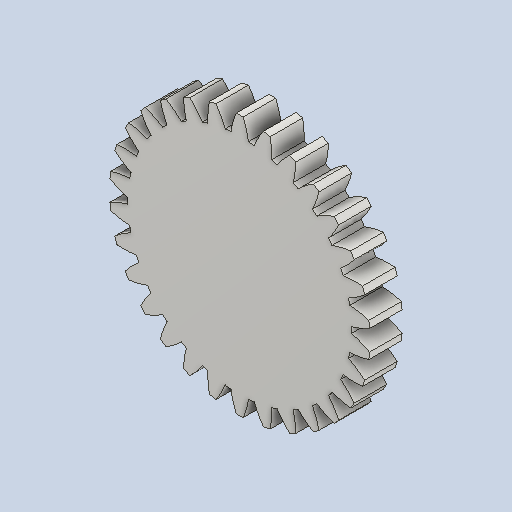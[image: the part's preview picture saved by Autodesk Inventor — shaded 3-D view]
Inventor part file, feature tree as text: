
AUTODESK INVENTOR PART (.ipt)
format: ipt  version: 2024 (Build 280153000, 153)  size: 265,728 bytes
history: native  units: mm (DEFAULTED — no unit token found)
features: plane x3, other x3, extrude x1, sketch x1
ambient origin geometry x8: Origin, YZ Plane, XZ Plane, XY Plane, X Axis, Y Axis, Z Axis, Center Point
bodies: Solid1 (feature_tree)
feature tree (8):
  extrude  "Extrusion1"  Depth=20.0mm TaperAngle=0.0deg
  plane  "Work Plane2"
  plane  "Work Plane8"
  plane  "Work Plane9"
  other  "Spur Gear"
  sketch  "Sketch1"  dims[d0=160.0mm d1=20.0mm d2=0.0mm d3=150.0mm d4=10.0mm d5=0.0mm d16=140.0mm d17=0.0mm d34=1.047198mm d39=0.0mm d41=0.0mm d43=140.0mm d46=140.0mm d47=0.0mm d48=0.0mm]
  other  "Srf1"
  other  "Pitch Diameter"
